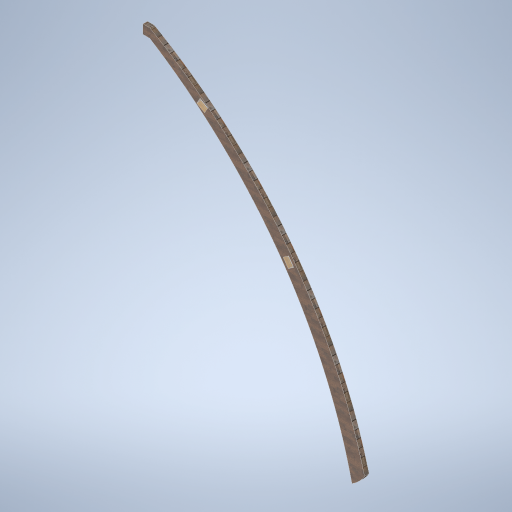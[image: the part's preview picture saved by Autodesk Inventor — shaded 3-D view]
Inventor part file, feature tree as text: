
AUTODESK INVENTOR PART (.ipt)
format: ipt  version: 2024.2 (Build 282272000, 272)  size: 309,760 bytes
history: native  units: mm
features: extrude x2, sketch x2
ambient origin geometry x8: Origin, YZ Plane, XZ Plane, XY Plane, X Axis, Y Axis, Z Axis, Center Point
bodies: Solid1 (feature_tree)
feature tree (4):
  extrude  "Extrusion1"  Depth=150.0mm
  extrude  "Extrusion2"  Depth=200.0mm
  sketch  "Sketch1"  dims[d0=10000.0mm d1=10000.0mm d2=150.0mm]
  sketch  "Sketch2"  dims[d3=100.0mm d4=0.0mm d5=200.0mm d6=30.0deg d7=150.0mm d8=200.0mm d9=9.599311mm d10=150.0mm d11=0.0mm d12=0.0mm]
